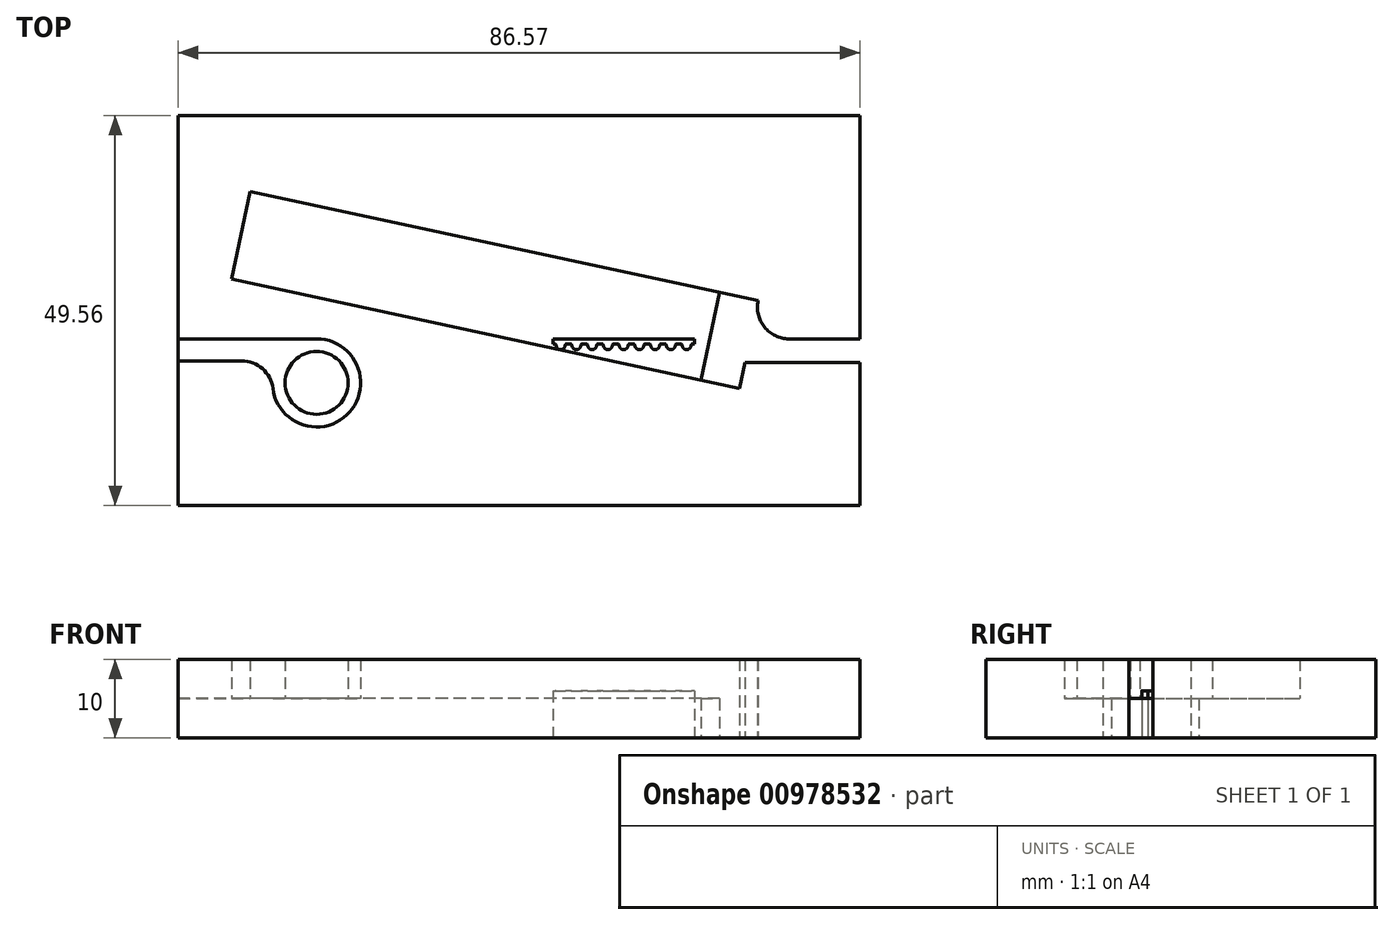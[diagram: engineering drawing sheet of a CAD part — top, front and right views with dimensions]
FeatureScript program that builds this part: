
annotation { "Feature Type Name" : "Feature", "Feature Type Description" : "" }
export const myFeature = defineFeature(function(context is Context, id is Id, definition is map)
    precondition{}
    {
        {
            var Q0;
            Q0=qCreatedBy(makeId("Top.planeOp"),FACE);
            var sketch = newSketch(context, id + "F0", { "sketchPlane" : qUnion([Q0])});
            skLineSegment(sketch, "E0", {"start": v(-98.86, 0) * mm, "end": v(98.86, 0) * mm, "construction": true});
            skPoint(sketch, "E1", {"position": v(0, 0) * mm});
            skLineSegment(sketch, "E2", {"start": v(-30, 0) * mm, "end": v(-47.57, 0) * mm});
            skCircle(sketch, "E3", {"center": v(-30, -5.6) * mm, "radius": 4 * mm});
            skLineSegment(sketch, "E4", {"start": v(-47.57, -2.8) * mm, "end": v(-39.52, -2.8) * mm});
            skArc(sketch, "E5", {"start": v(-35.56, -6.3) * mm, "mid": v(-36.88, -3.8) * mm, "end": v(-39.52, -2.8) * mm});
            skArc(sketch, "E6", {"start": v(-35.56, -6.3) * mm, "mid": v(-25.8, -9.3) * mm, "end": v(-30, 0) * mm});
            skArc(sketch, "E7", {"start": v(-30, 0) * mm, "mid": v(-34.2, -1.9) * mm, "end": v(-35.56, -6.3) * mm, "construction": true});
            skCircle(sketch, "E8", {"center": v(30, 4) * mm, "radius": 4 * mm});
            skLineSegment(sketch, "E9", {"start": v(-15.64, 9.7) * mm, "end": v(29.16, 0.09) * mm, "construction": true});
            skCircle(sketch, "E10", {"center": v(-30, -5.6) * mm, "radius": 10.6 * mm, "construction": true});
            skLineSegment(sketch, "E11", {"start": v(5.56, 9.25) * mm, "end": v(21.2, 5.89) * mm});
            skLineSegment(sketch, "E12", {"start": v(3.17, -1.88) * mm, "end": v(18.81, -5.24) * mm});
            skLineSegment(sketch, "E13", {"start": v(18.81, -5.24) * mm, "end": v(21.2, 5.89) * mm});
            skLineSegment(sketch, "E14", {"start": v(3.17, -1.88) * mm, "end": v(5.56, 9.25) * mm, "construction": true});
            skLineSegment(sketch, "E15", {"start": v(5.56, 9.25) * mm, "end": v(-14, 13.45) * mm});
            skLineSegment(sketch, "E16", {"start": v(3.17, -1.88) * mm, "end": v(-16.39, 2.32) * mm});
            skLineSegment(sketch, "E17", {"start": v(-14.56, 10.82) * mm, "end": v(-15.82, 4.95) * mm});
            skLineSegment(sketch, "E18", {"start": v(-14.56, 10.82) * mm, "end": v(-17.2, 11.38) * mm});
            skLineSegment(sketch, "E19", {"start": v(-17.2, 11.38) * mm, "end": v(-18.46, 5.52) * mm});
            skLineSegment(sketch, "E20", {"start": v(-17.83, 8.45) * mm, "end": v(-15.2, 7.88) * mm, "construction": true});
            skPoint(sketch, "E21", {"position": v(-15.2, 7.88) * mm});
            skLineSegment(sketch, "E22", {"start": v(-18.46, 5.52) * mm, "end": v(-15.82, 4.95) * mm});
            skLineSegment(sketch, "E23", {"start": v(-14, 13.45) * mm, "end": v(-21.53, 15.06) * mm});
            skLineSegment(sketch, "E24", {"start": v(-16.39, 2.32) * mm, "end": v(-23.91, 3.94) * mm});
            skLineSegment(sketch, "E25", {"start": v(-21.53, 15.06) * mm, "end": v(-23.91, 3.94) * mm});
            skLineSegment(sketch, "E26", {"start": v(-15.2, 7.88) * mm, "end": v(-44.52, 14.18) * mm, "construction": true});
            skLineSegment(sketch, "E27", {"start": v(-47.57, 0) * mm, "end": v(-41.48, 28.36) * mm});
            skPoint(sketch, "E28", {"position": v(-44.52, 14.18) * mm});
            skLineSegment(sketch, "E29", {"start": v(-47.57, 0) * mm, "end": v(-47.57, -21.2) * mm});
            skLineSegment(sketch, "E30", {"start": v(-47.57, -21.2) * mm, "end": v(39, -21.2) * mm});
            skLineSegment(sketch, "E31", {"start": v(39, -21.2) * mm, "end": v(39, 28.36) * mm});
            skLineSegment(sketch, "E32", {"start": v(39, 28.36) * mm, "end": v(-41.48, 28.36) * mm});
            skLineSegment(sketch, "E33", {"start": v(-23.91, 3.94) * mm, "end": v(-40.83, 7.57) * mm});
            skLineSegment(sketch, "E34", {"start": v(-21.53, 15.06) * mm, "end": v(-38.44, 18.7) * mm});
            skLineSegment(sketch, "E35.trimOffspring", {"start": v(-40.83, 7.57) * mm, "end": v(-38.44, 18.7) * mm});
            skLineSegment(sketch, "E36", {"start": v(21.2, 5.89) * mm, "end": v(26.09, 4.84) * mm});
            skLineSegment(sketch, "E37", {"start": v(30, 0) * mm, "end": v(39, 0) * mm});
            skLineSegment(sketch, "E38", {"start": v(39, -3) * mm, "end": v(24.4, -3) * mm});
            skLineSegment(sketch, "E39", {"start": v(26.09, 4.84) * mm, "end": v(24.4, -3) * mm, "construction": true});
            skLineSegment(sketch, "E40", {"start": v(24.4, -3) * mm, "end": v(23.7, -6.29) * mm});
            skLineSegment(sketch, "E41", {"start": v(18.81, -5.24) * mm, "end": v(23.7, -6.29) * mm});
            skLineSegment(sketch, "E42", {"start": v(-47.57, 0) * mm, "end": v(-47.57, 28.36) * mm});
            skLineSegment(sketch, "E43", {"start": v(-47.57, 28.36) * mm, "end": v(-41.48, 28.36) * mm});
            skSolve(sketch);
        }
        {
            var Q0;
            Q0=makeQuery(id+"F0.imprint","IMPRINT",FACE,{"disambiguationData":[TD([[makeQuery(id+"F0.imprint","IMPRINT",EDGE,{"derivedFrom":sQuery(id+"F0.wireOp",EDGE,"E2")}),-1.0]])]});
            var Q1;
            {var subQ0=sQuery(id+"F0.wireOp",EDGE,"E8");var subQ1=makeQuery(id+"F0.imprint","INTERSECT",VERTEX,{"derivedFrom":[subQ0,sQuery(id+"F0.wireOp",EDGE,"E36")]});Q1=makeQuery(id+"F0.imprint","IMPRINT",FACE,{"disambiguationData":[TD([[makeQuery(id+"F0.imprint","IMPRINT",EDGE,{"disambiguationData":[TD([[subQ1,-1.0]])],"derivedFrom":subQ0}),1.0]])]});}
            var Q2;
            Q2=makeQuery(id+"F0.imprint","IMPRINT",FACE,{"disambiguationData":[TD([[makeQuery(id+"F0.imprint","IMPRINT",EDGE,{"derivedFrom":sQuery(id+"F0.wireOp",EDGE,"E3")}),1.0]])]});
            var Q3;
            Q3=makeQuery(id+"F0.imprint","IMPRINT",FACE,{"disambiguationData":[TD([[makeQuery(id+"F0.imprint","IMPRINT",EDGE,{"derivedFrom":sQuery(id+"F0.wireOp",EDGE,"E27")}),1.0]])]});
            extrude(context, id + "F1", {"entities" : qUnion([Q0, Q1, Q2, Q3]), "depth" : 10 * mm, "offsetDistance" : 25 * mm});
        }
        {
            var Q0;
            {var subQ1=sQuery(id+"F0.wireOp",EDGE,"E2");Q0=makeQuery(id+"F0.imprint","IMPRINT",FACE,{"disambiguationData":[TD([[makeQuery(id+"F0.imprint","IMPRINT",EDGE,{"derivedFrom":subQ1}),1.0]])]});}
            var Q1;
            Q1=makeQuery(id+"F0.imprint","IMPRINT",FACE,{"disambiguationData":[TD([[makeQuery(id+"F0.imprint","IMPRINT",EDGE,{"derivedFrom":sQuery(id+"F0.wireOp",EDGE,"E25")}),-1.0]])]});
            var Q2;
            Q2=makeQuery(id+"F0.imprint","IMPRINT",FACE,{"disambiguationData":[TD([[makeQuery(id+"F0.imprint","IMPRINT",EDGE,{"derivedFrom":sQuery(id+"F0.wireOp",EDGE,"E11")}),-1.0]])]});
            var Q3;
            Q3=makeQuery(id+"F0.imprint","IMPRINT",FACE,{"disambiguationData":[TD([[makeQuery(id+"F0.imprint","IMPRINT",EDGE,{"derivedFrom":sQuery(id+"F0.wireOp",EDGE,"E17")}),-1.0]])]});
            extrude(context, id + "F2", {"entities" : qUnion([Q0, Q1, Q2, Q3]), "operationType" : NewBodyOperationType.ADD, "depth" : 5 * mm, "offsetDistance" : 25 * mm});
        }
        {
            var Q0;
            Q0=qCreatedBy(makeId("Top.planeOp"),FACE);
            var sketch = newSketch(context, id + "F3", { "sketchPlane" : qUnion([Q0])});
            skLineSegment(sketch, "E44", {"start": v(-1, 0) * mm, "end": v(1, 0) * mm});
            skLineSegment(sketch, "E45", {"start": v(-1, -1.38) * mm, "end": v(1, -1.38) * mm, "construction": true});
            skLineSegment(sketch, "E46", {"start": v(-1, 0) * mm, "end": v(-1, -1.38) * mm, "construction": true});
            skLineSegment(sketch, "E47", {"start": v(1, 0) * mm, "end": v(1, -1.38) * mm, "construction": true});
            skArc(sketch, "E48", {"start": v(0.5, -1.07) * mm, "mid": v(0.7, -1.3) * mm, "end": v(1, -1.38) * mm});
            skArc(sketch, "E49", {"start": v(0.4, -0.76) * mm, "mid": v(0.44, -0.92) * mm, "end": v(0.5, -1.07) * mm});
            skLineSegment(sketch, "E50", {"start": v(0, 0) * mm, "end": v(0, -1.38) * mm, "construction": true});
            skLineSegment(sketch, "E51", {"start": v(0, -0.63) * mm, "end": v(0.26, -0.63) * mm});
            skArc(sketch, "E52", {"start": v(0.4, -0.76) * mm, "mid": v(0.36, -0.67) * mm, "end": v(0.26, -0.63) * mm});
            skLineSegment(sketch, "E53.MirrorCS", {"start": v(0, -0.63) * mm, "end": v(-0.26, -0.63) * mm});
            skArc(sketch, "E54.MirrorCS", {"start": v(-0.4, -0.76) * mm, "mid": v(-0.36, -0.67) * mm, "end": v(-0.26, -0.63) * mm});
            skArc(sketch, "E55.MirrorCS", {"start": v(-0.4, -0.76) * mm, "mid": v(-0.44, -0.92) * mm, "end": v(-0.5, -1.07) * mm});
            skArc(sketch, "E56.MirrorCS", {"start": v(-0.5, -1.07) * mm, "mid": v(-0.7, -1.3) * mm, "end": v(-1, -1.38) * mm});
            skLineSegment(sketch, "E57.1.0.0", {"start": v(1, 0) * mm, "end": v(3, 0) * mm});
            skArc(sketch, "E57.1.0.1", {"start": v(1.5, -1.07) * mm, "mid": v(1.3, -1.3) * mm, "end": v(1, -1.38) * mm});
            skArc(sketch, "E57.1.0.2", {"start": v(1.6, -0.76) * mm, "mid": v(1.56, -0.92) * mm, "end": v(1.5, -1.07) * mm});
            skArc(sketch, "E57.1.0.3", {"start": v(1.6, -0.76) * mm, "mid": v(1.64, -0.67) * mm, "end": v(1.74, -0.63) * mm});
            skLineSegment(sketch, "E57.1.0.4", {"start": v(2, -0.63) * mm, "end": v(1.74, -0.63) * mm});
            skLineSegment(sketch, "E57.1.0.5", {"start": v(2, -0.63) * mm, "end": v(2.26, -0.63) * mm});
            skArc(sketch, "E57.1.0.6", {"start": v(2.4, -0.76) * mm, "mid": v(2.36, -0.67) * mm, "end": v(2.26, -0.63) * mm});
            skArc(sketch, "E57.1.0.7", {"start": v(2.4, -0.76) * mm, "mid": v(2.44, -0.92) * mm, "end": v(2.5, -1.07) * mm});
            skArc(sketch, "E57.1.0.8", {"start": v(2.5, -1.07) * mm, "mid": v(2.7, -1.3) * mm, "end": v(3, -1.38) * mm});
            skLineSegment(sketch, "E57.2.0.0", {"start": v(3, 0) * mm, "end": v(5, 0) * mm});
            skArc(sketch, "E57.2.0.1", {"start": v(3.5, -1.07) * mm, "mid": v(3.3, -1.3) * mm, "end": v(3, -1.38) * mm});
            skArc(sketch, "E57.2.0.2", {"start": v(3.6, -0.76) * mm, "mid": v(3.56, -0.92) * mm, "end": v(3.5, -1.07) * mm});
            skArc(sketch, "E57.2.0.3", {"start": v(3.6, -0.76) * mm, "mid": v(3.64, -0.67) * mm, "end": v(3.74, -0.63) * mm});
            skLineSegment(sketch, "E57.2.0.4", {"start": v(4, -0.63) * mm, "end": v(3.74, -0.63) * mm});
            skLineSegment(sketch, "E57.2.0.5", {"start": v(4, -0.63) * mm, "end": v(4.26, -0.63) * mm});
            skArc(sketch, "E57.2.0.6", {"start": v(4.4, -0.76) * mm, "mid": v(4.36, -0.67) * mm, "end": v(4.26, -0.63) * mm});
            skArc(sketch, "E57.2.0.7", {"start": v(4.4, -0.76) * mm, "mid": v(4.44, -0.92) * mm, "end": v(4.5, -1.07) * mm});
            skArc(sketch, "E57.2.0.8", {"start": v(4.5, -1.07) * mm, "mid": v(4.7, -1.3) * mm, "end": v(5, -1.38) * mm});
            skLineSegment(sketch, "E57.3.0.0", {"start": v(5, 0) * mm, "end": v(7, 0) * mm});
            skArc(sketch, "E57.3.0.1", {"start": v(5.5, -1.07) * mm, "mid": v(5.3, -1.3) * mm, "end": v(5, -1.38) * mm});
            skArc(sketch, "E57.3.0.2", {"start": v(5.6, -0.76) * mm, "mid": v(5.56, -0.92) * mm, "end": v(5.5, -1.07) * mm});
            skArc(sketch, "E57.3.0.3", {"start": v(5.6, -0.76) * mm, "mid": v(5.64, -0.67) * mm, "end": v(5.74, -0.63) * mm});
            skLineSegment(sketch, "E57.3.0.4", {"start": v(6, -0.63) * mm, "end": v(5.74, -0.63) * mm});
            skLineSegment(sketch, "E57.3.0.5", {"start": v(6, -0.63) * mm, "end": v(6.26, -0.63) * mm});
            skArc(sketch, "E57.3.0.6", {"start": v(6.4, -0.76) * mm, "mid": v(6.36, -0.67) * mm, "end": v(6.26, -0.63) * mm});
            skArc(sketch, "E57.3.0.7", {"start": v(6.4, -0.76) * mm, "mid": v(6.44, -0.92) * mm, "end": v(6.5, -1.07) * mm});
            skArc(sketch, "E57.3.0.8", {"start": v(6.5, -1.07) * mm, "mid": v(6.7, -1.3) * mm, "end": v(7, -1.38) * mm});
            skLineSegment(sketch, "E57.4.0.0", {"start": v(7, 0) * mm, "end": v(9, 0) * mm});
            skArc(sketch, "E57.4.0.1", {"start": v(7.5, -1.07) * mm, "mid": v(7.3, -1.3) * mm, "end": v(7, -1.38) * mm});
            skArc(sketch, "E57.4.0.2", {"start": v(7.6, -0.76) * mm, "mid": v(7.56, -0.92) * mm, "end": v(7.5, -1.07) * mm});
            skArc(sketch, "E57.4.0.3", {"start": v(7.6, -0.76) * mm, "mid": v(7.64, -0.67) * mm, "end": v(7.74, -0.63) * mm});
            skLineSegment(sketch, "E57.4.0.4", {"start": v(8, -0.63) * mm, "end": v(7.74, -0.63) * mm});
            skLineSegment(sketch, "E57.4.0.5", {"start": v(8, -0.63) * mm, "end": v(8.26, -0.63) * mm});
            skArc(sketch, "E57.4.0.6", {"start": v(8.4, -0.76) * mm, "mid": v(8.36, -0.67) * mm, "end": v(8.26, -0.63) * mm});
            skArc(sketch, "E57.4.0.7", {"start": v(8.4, -0.76) * mm, "mid": v(8.44, -0.92) * mm, "end": v(8.5, -1.07) * mm});
            skArc(sketch, "E57.4.0.8", {"start": v(8.5, -1.07) * mm, "mid": v(8.7, -1.3) * mm, "end": v(9, -1.38) * mm});
            skLineSegment(sketch, "E57.5.0.0", {"start": v(9, 0) * mm, "end": v(11, 0) * mm});
            skArc(sketch, "E57.5.0.1", {"start": v(9.5, -1.07) * mm, "mid": v(9.3, -1.3) * mm, "end": v(9, -1.38) * mm});
            skArc(sketch, "E57.5.0.2", {"start": v(9.6, -0.76) * mm, "mid": v(9.56, -0.92) * mm, "end": v(9.5, -1.07) * mm});
            skArc(sketch, "E57.5.0.3", {"start": v(9.6, -0.76) * mm, "mid": v(9.64, -0.67) * mm, "end": v(9.74, -0.63) * mm});
            skLineSegment(sketch, "E57.5.0.4", {"start": v(10, -0.63) * mm, "end": v(9.74, -0.63) * mm});
            skLineSegment(sketch, "E57.5.0.5", {"start": v(10, -0.63) * mm, "end": v(10.26, -0.63) * mm});
            skArc(sketch, "E57.5.0.6", {"start": v(10.4, -0.76) * mm, "mid": v(10.36, -0.67) * mm, "end": v(10.26, -0.63) * mm});
            skArc(sketch, "E57.5.0.7", {"start": v(10.4, -0.76) * mm, "mid": v(10.44, -0.92) * mm, "end": v(10.5, -1.07) * mm});
            skArc(sketch, "E57.5.0.8", {"start": v(10.5, -1.07) * mm, "mid": v(10.7, -1.3) * mm, "end": v(11, -1.38) * mm});
            skLineSegment(sketch, "E57.6.0.0", {"start": v(11, 0) * mm, "end": v(13, 0) * mm});
            skArc(sketch, "E57.6.0.1", {"start": v(11.5, -1.07) * mm, "mid": v(11.3, -1.3) * mm, "end": v(11, -1.38) * mm});
            skArc(sketch, "E57.6.0.2", {"start": v(11.6, -0.76) * mm, "mid": v(11.56, -0.92) * mm, "end": v(11.5, -1.07) * mm});
            skArc(sketch, "E57.6.0.3", {"start": v(11.6, -0.76) * mm, "mid": v(11.64, -0.67) * mm, "end": v(11.74, -0.63) * mm});
            skLineSegment(sketch, "E57.6.0.4", {"start": v(12, -0.63) * mm, "end": v(11.74, -0.63) * mm});
            skLineSegment(sketch, "E57.6.0.5", {"start": v(12, -0.63) * mm, "end": v(12.26, -0.63) * mm});
            skArc(sketch, "E57.6.0.6", {"start": v(12.4, -0.76) * mm, "mid": v(12.36, -0.67) * mm, "end": v(12.26, -0.63) * mm});
            skArc(sketch, "E57.6.0.7", {"start": v(12.4, -0.76) * mm, "mid": v(12.44, -0.92) * mm, "end": v(12.5, -1.07) * mm});
            skArc(sketch, "E57.6.0.8", {"start": v(12.5, -1.07) * mm, "mid": v(12.7, -1.3) * mm, "end": v(13, -1.38) * mm});
            skLineSegment(sketch, "E57.7.0.0", {"start": v(13, 0) * mm, "end": v(15, 0) * mm});
            skArc(sketch, "E57.7.0.1", {"start": v(13.5, -1.07) * mm, "mid": v(13.3, -1.3) * mm, "end": v(13, -1.38) * mm});
            skArc(sketch, "E57.7.0.2", {"start": v(13.6, -0.76) * mm, "mid": v(13.56, -0.92) * mm, "end": v(13.5, -1.07) * mm});
            skArc(sketch, "E57.7.0.3", {"start": v(13.6, -0.76) * mm, "mid": v(13.64, -0.67) * mm, "end": v(13.74, -0.63) * mm});
            skLineSegment(sketch, "E57.7.0.4", {"start": v(14, -0.63) * mm, "end": v(13.74, -0.63) * mm});
            skLineSegment(sketch, "E57.7.0.5", {"start": v(14, -0.63) * mm, "end": v(14.26, -0.63) * mm});
            skArc(sketch, "E57.7.0.6", {"start": v(14.4, -0.76) * mm, "mid": v(14.36, -0.67) * mm, "end": v(14.26, -0.63) * mm});
            skArc(sketch, "E57.7.0.7", {"start": v(14.4, -0.76) * mm, "mid": v(14.44, -0.92) * mm, "end": v(14.5, -1.07) * mm});
            skArc(sketch, "E57.7.0.8", {"start": v(14.5, -1.07) * mm, "mid": v(14.7, -1.3) * mm, "end": v(15, -1.38) * mm});
            skLineSegment(sketch, "E57.8.0.0", {"start": v(15, 0) * mm, "end": v(17, 0) * mm});
            skArc(sketch, "E57.8.0.1", {"start": v(15.5, -1.07) * mm, "mid": v(15.3, -1.3) * mm, "end": v(15, -1.38) * mm});
            skArc(sketch, "E57.8.0.2", {"start": v(15.6, -0.76) * mm, "mid": v(15.56, -0.92) * mm, "end": v(15.5, -1.07) * mm});
            skArc(sketch, "E57.8.0.3", {"start": v(15.6, -0.76) * mm, "mid": v(15.64, -0.67) * mm, "end": v(15.74, -0.63) * mm});
            skLineSegment(sketch, "E57.8.0.4", {"start": v(16, -0.63) * mm, "end": v(15.74, -0.63) * mm});
            skLineSegment(sketch, "E57.8.0.5", {"start": v(16, -0.63) * mm, "end": v(16.26, -0.63) * mm});
            skArc(sketch, "E57.8.0.6", {"start": v(16.4, -0.76) * mm, "mid": v(16.36, -0.67) * mm, "end": v(16.26, -0.63) * mm});
            skArc(sketch, "E57.8.0.7", {"start": v(16.4, -0.76) * mm, "mid": v(16.44, -0.92) * mm, "end": v(16.5, -1.07) * mm});
            skArc(sketch, "E57.8.0.8", {"start": v(16.5, -1.07) * mm, "mid": v(16.7, -1.3) * mm, "end": v(17, -1.38) * mm});
            skLineSegment(sketch, "E57.9.0.0", {"start": v(17, 0) * mm, "end": v(19, 0) * mm});
            skArc(sketch, "E57.9.0.1", {"start": v(17.5, -1.07) * mm, "mid": v(17.3, -1.3) * mm, "end": v(17, -1.38) * mm});
            skArc(sketch, "E57.9.0.2", {"start": v(17.6, -0.76) * mm, "mid": v(17.56, -0.92) * mm, "end": v(17.5, -1.07) * mm});
            skArc(sketch, "E57.9.0.3", {"start": v(17.6, -0.76) * mm, "mid": v(17.64, -0.67) * mm, "end": v(17.74, -0.63) * mm});
            skLineSegment(sketch, "E57.9.0.4", {"start": v(18, -0.63) * mm, "end": v(17.74, -0.63) * mm});
            skLineSegment(sketch, "E57.9.0.5", {"start": v(18, -0.63) * mm, "end": v(18.26, -0.63) * mm});
            skArc(sketch, "E57.9.0.6", {"start": v(18.4, -0.76) * mm, "mid": v(18.36, -0.67) * mm, "end": v(18.26, -0.63) * mm});
            skArc(sketch, "E57.9.0.7", {"start": v(18.4, -0.76) * mm, "mid": v(18.44, -0.92) * mm, "end": v(18.5, -1.07) * mm});
            skArc(sketch, "E57.9.0.8", {"start": v(18.5, -1.07) * mm, "mid": v(18.7, -1.3) * mm, "end": v(19, -1.38) * mm});
            skLineSegment(sketch, "E57.direction1", {"start": v(-1, 0) * mm, "end": v(1, 0) * mm, "construction": true});
            skLineSegment(sketch, "E58", {"start": v(-1, 0) * mm, "end": v(-1, -1.38) * mm});
            skLineSegment(sketch, "E59", {"start": v(0, -0.63) * mm, "end": v(0, 0) * mm});
            skLineSegment(sketch, "E60", {"start": v(18, -0.63) * mm, "end": v(18, 0) * mm});
            skSolve(sketch);
        }
        {
            var Q0;
            Q0=makeQuery(id+"F3.imprint","IMPRINT",FACE,{"disambiguationData":[TD([[makeQuery(id+"F3.imprint","IMPRINT",EDGE,{"derivedFrom":sQuery(id+"F3.wireOp",EDGE,"E48")}),1.0]])]});
            extrude(context, id + "F4", {"entities" : qUnion([Q0]), "depth" : 6 * mm, "offsetDistance" : 25 * mm});
        }
    });
